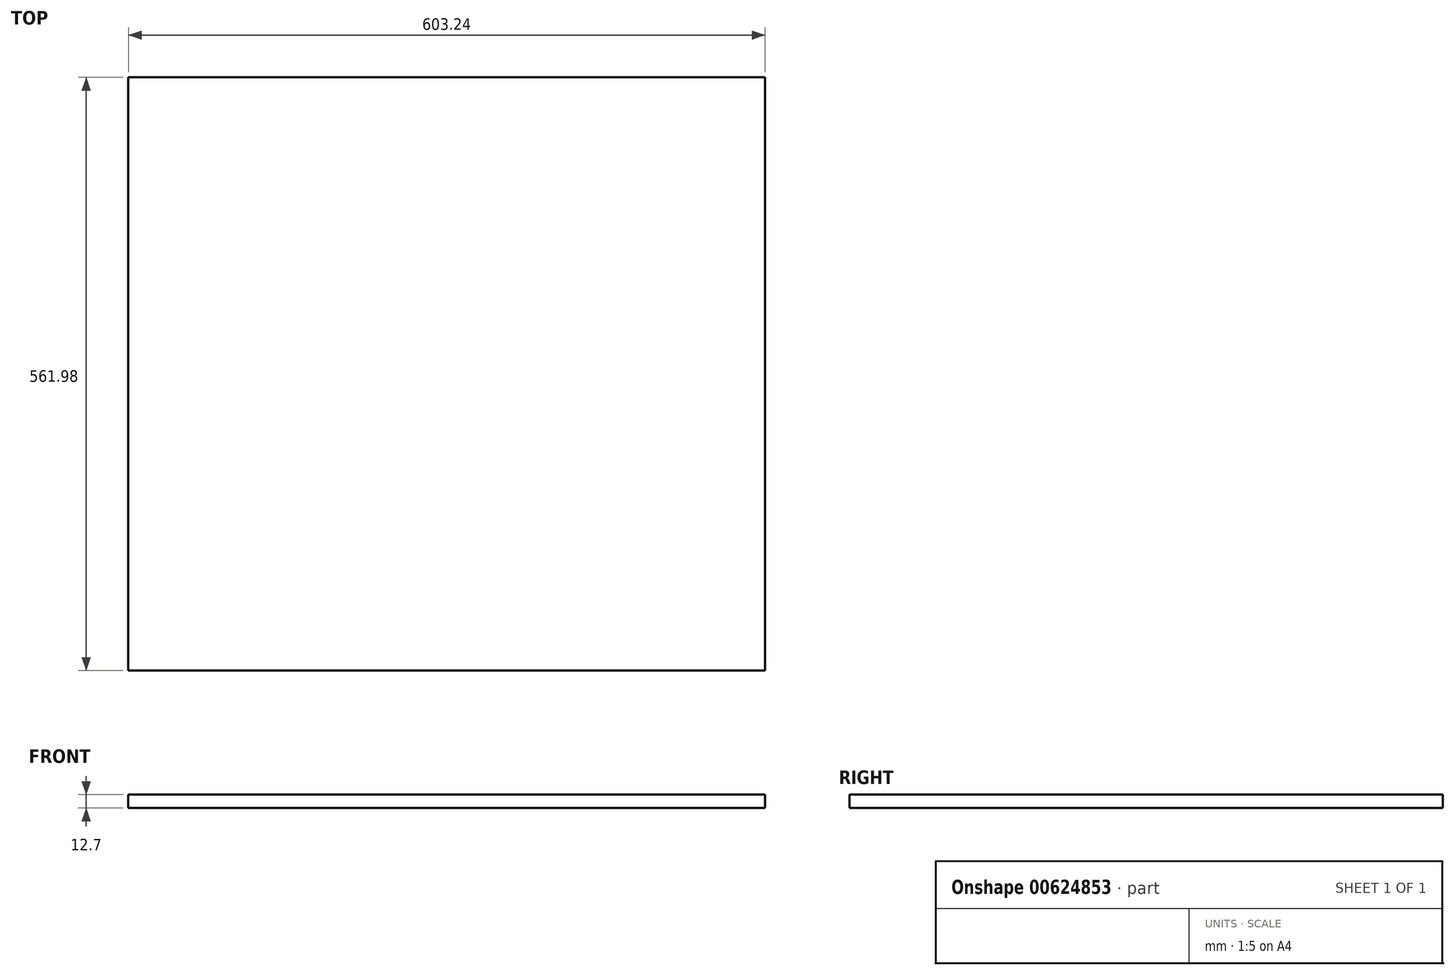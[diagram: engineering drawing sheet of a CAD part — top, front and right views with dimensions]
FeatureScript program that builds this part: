
annotation { "Feature Type Name" : "Feature", "Feature Type Description" : "" }
export const myFeature = defineFeature(function(context is Context, id is Id, definition is map)
    precondition{}
    {
        {
            var Q0;
            Q0=qCreatedBy(makeId("Top.planeOp"),FACE);
            var sketch = newSketch(context, id + "F0", { "sketchPlane" : qUnion([Q0])});
            skLineSegment(sketch, "E0.bottom", {"start": v(-301.63, 280.99) * mm, "end": v(301.63, 280.99) * mm});
            skLineSegment(sketch, "E0.top", {"start": v(-301.63, -280.99) * mm, "end": v(301.63, -280.99) * mm});
            skLineSegment(sketch, "E0.left", {"start": v(-301.63, 280.99) * mm, "end": v(-301.63, -280.99) * mm});
            skLineSegment(sketch, "E0.right", {"start": v(301.63, 280.99) * mm, "end": v(301.62, -280.99) * mm});
            skPoint(sketch, "E0.middle", {"position": v(0, 0) * mm});
            skSolve(sketch);
        }
        {
            var Q0;
            Q0=qSketchRegion(id+"F0",true);
            extrude(context, id + "F1", {"entities" : qUnion([Q0]), "oppositeDirection" : true, "depth" : 12.7 * mm, "offsetDistance" : 25.4 * mm});
        }
    });
